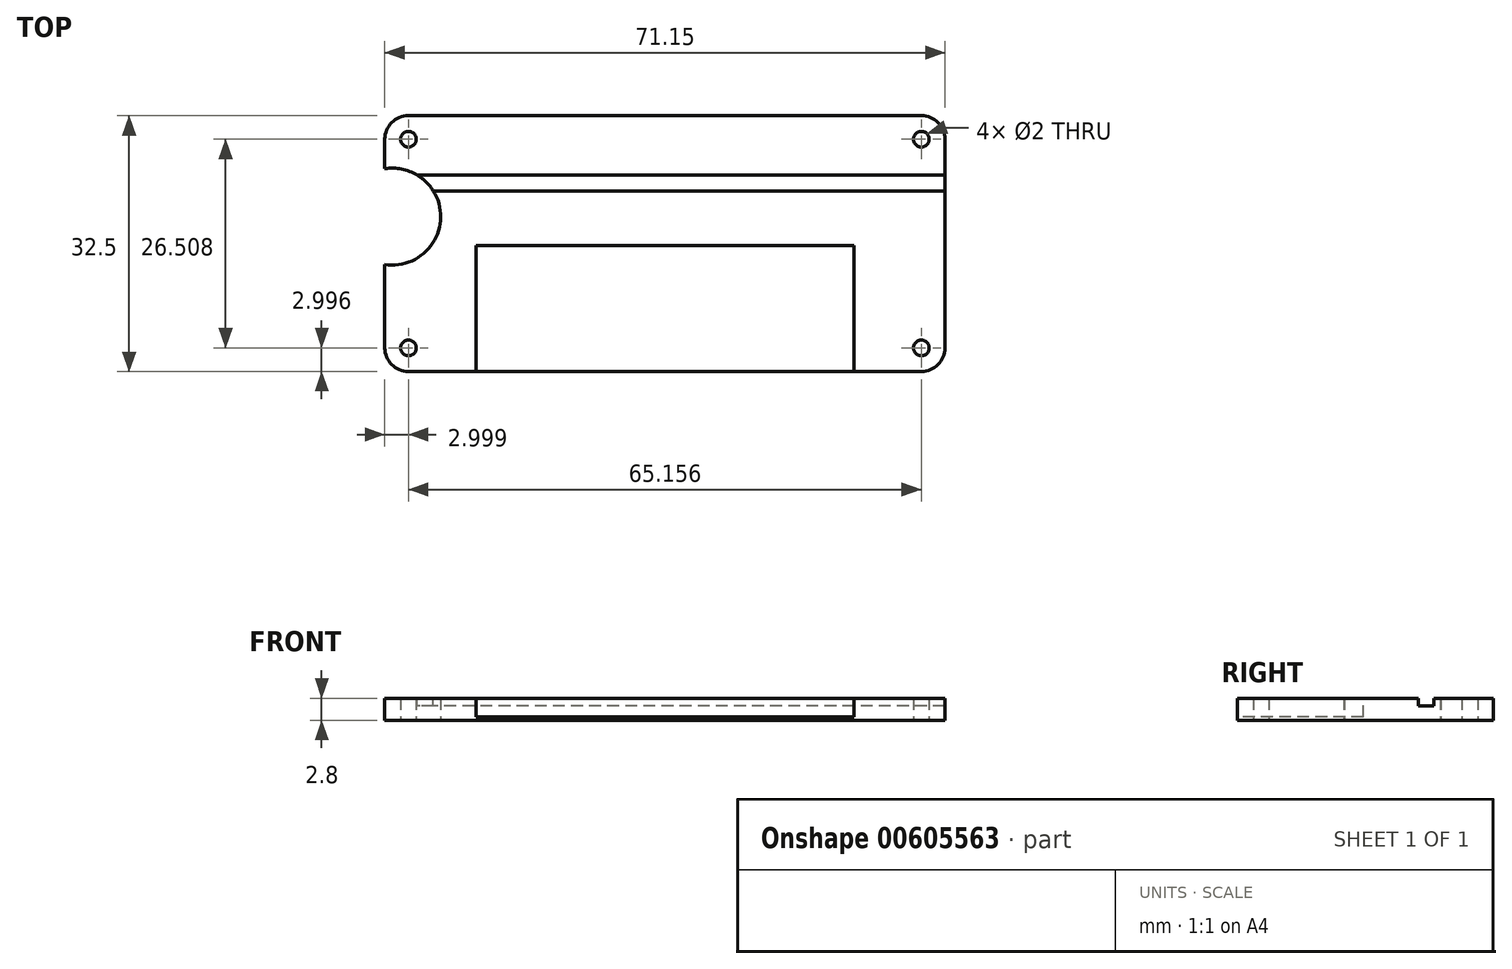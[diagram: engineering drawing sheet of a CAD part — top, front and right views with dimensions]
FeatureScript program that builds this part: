
annotation { "Feature Type Name" : "Feature", "Feature Type Description" : "" }
export const myFeature = defineFeature(function(context is Context, id is Id, definition is map)
    precondition{}
    {
        {
            var Q0;
            Q0=qCreatedBy(makeId("Top.planeOp"),FACE);
            var sketch = newSketch(context, id + "F0", { "sketchPlane" : qUnion([Q0])});
            skCircle(sketch, "E0", {"center": v(-35.08, 4.05) * mm, "radius": 2.5 * mm, "construction": true});
            skLineSegment(sketch, "E1", {"start": v(-0.75, 33.18) * mm, "end": v(-0.75, -27.99) * mm, "construction": true});
            skLineSegment(sketch, "E2", {"start": v(-39.9, 0.38) * mm, "end": v(50.97, 0.38) * mm, "construction": true});
            skCircle(sketch, "E3", {"center": v(-33.25, 13.52) * mm, "radius": 3 * mm, "construction": true});
            skLineSegment(sketch, "E4.bottom", {"start": v(-33.25, 13.52) * mm, "end": v(31.75, 13.52) * mm, "construction": true});
            skLineSegment(sketch, "E4.top", {"start": v(-33.25, -12.75) * mm, "end": v(31.75, -12.75) * mm, "construction": true});
            skLineSegment(sketch, "E4.left", {"start": v(-33.25, 13.52) * mm, "end": v(-33.25, -12.75) * mm, "construction": true});
            skLineSegment(sketch, "E4.right", {"start": v(31.75, 13.52) * mm, "end": v(31.75, -12.75) * mm, "construction": true});
            skCircle(sketch, "E5", {"center": v(31.75, 13.52) * mm, "radius": 3 * mm, "construction": true});
            skCircle(sketch, "E6", {"center": v(31.75, -12.75) * mm, "radius": 3 * mm, "construction": true});
            skCircle(sketch, "E7", {"center": v(-33.25, -12.75) * mm, "radius": 3 * mm, "construction": true});
            skLineSegment(sketch, "E8", {"start": v(-33.25, -12.75) * mm, "end": v(31.75, 13.52) * mm});
            skLineSegment(sketch, "E9", {"start": v(31.75, -12.75) * mm, "end": v(-33.25, 13.52) * mm});
            skLineSegment(sketch, "E10.bottom", {"start": v(31.82, 16.63) * mm, "end": v(-33.33, 16.63) * mm});
            skLineSegment(sketch, "E10.top", {"start": v(31.82, -15.87) * mm, "end": v(-33.33, -15.87) * mm});
            skLineSegment(sketch, "E10.left", {"start": v(34.82, 13.63) * mm, "end": v(34.82, -12.87) * mm});
            skLineSegment(sketch, "E10.right", {"start": v(-36.33, 13.63) * mm, "end": v(-36.33, -12.87) * mm, "construction": true});
            skPoint(sketch, "E10.middle", {"position": v(-0.75, 0.38) * mm});
            skPoint(sketch, "E11.visualSharp", {"position": v(-36.33, 16.63) * mm});
            skArc(sketch, "E11.filletArc", {"start": v(-33.33, 16.63) * mm, "mid": v(-35.45, 15.76) * mm, "end": v(-36.33, 13.63) * mm});
            skPoint(sketch, "E12.visualSharp", {"position": v(-36.33, -15.87) * mm});
            skArc(sketch, "E12.filletArc", {"start": v(-36.33, -12.87) * mm, "mid": v(-35.45, -15) * mm, "end": v(-33.33, -15.87) * mm});
            skPoint(sketch, "E13.visualSharp", {"position": v(34.82, -15.87) * mm});
            skArc(sketch, "E13.filletArc", {"start": v(31.82, -15.87) * mm, "mid": v(33.95, -15) * mm, "end": v(34.82, -12.87) * mm});
            skPoint(sketch, "E14.visualSharp", {"position": v(34.82, 16.63) * mm});
            skArc(sketch, "E14.filletArc", {"start": v(34.82, 13.63) * mm, "mid": v(33.95, 15.76) * mm, "end": v(31.82, 16.63) * mm});
            skArc(sketch, "E15", {"start": v(-36.33, -2.26) * mm, "mid": v(-29.23, 3.81) * mm, "end": v(-36.33, 9.88) * mm});
            skLineSegment(sketch, "E16", {"start": v(-36.33, 13.63) * mm, "end": v(-36.33, 9.88) * mm});
            skLineSegment(sketch, "E17", {"start": v(-36.33, -12.87) * mm, "end": v(-36.33, -2.26) * mm});
            skCircle(sketch, "E18", {"center": v(-33.33, 13.63) * mm, "radius": 1 * mm});
            skCircle(sketch, "E19", {"center": v(31.82, 13.63) * mm, "radius": 1 * mm});
            skCircle(sketch, "E20", {"center": v(31.82, -12.87) * mm, "radius": 1 * mm});
            skCircle(sketch, "E21", {"center": v(-33.33, -12.87) * mm, "radius": 1 * mm});
            skSolve(sketch);
        }
        {
            var Q0;
            Q0=makeQuery(id+"F0.imprint","IMPRINT",FACE,{"disambiguationData":[TD([[makeQuery(id+"F0.imprint","IMPRINT",EDGE,{"derivedFrom":sQuery(id+"F0.wireOp",EDGE,"E10.bottom")}),1.0]])]});
            extrude(context, id + "F1", {"entities" : qUnion([Q0]), "depth" : 2.8 * mm, "offsetDistance" : 25 * mm});
        }
        {
            var Q0;
            Q0=makeQuery(id+"F1.opExtrude","CAP_FACE",FACE,{"disambiguationData":[OSD([sQuery(id+"F0.wireOp",EDGE,"E10.bottom"),sQuery(id+"F0.wireOp",EDGE,"E10.top"),sQuery(id+"F0.wireOp",EDGE,"E10.left"),sQuery(id+"F0.wireOp",EDGE,"E11.filletArc"),sQuery(id+"F0.wireOp",EDGE,"E12.filletArc"),sQuery(id+"F0.wireOp",EDGE,"E13.filletArc"),sQuery(id+"F0.wireOp",EDGE,"E14.filletArc"),sQuery(id+"F0.wireOp",EDGE,"E15"),sQuery(id+"F0.wireOp",EDGE,"E16"),sQuery(id+"F0.wireOp",EDGE,"E17"),sQuery(id+"F0.wireOp",EDGE,"E18"),sQuery(id+"F0.wireOp",EDGE,"E19"),sQuery(id+"F0.wireOp",EDGE,"E20"),sQuery(id+"F0.wireOp",EDGE,"E21")])],"isStart":false});
            var sketch = newSketch(context, id + "F2", { "sketchPlane" : qUnion([Q0])});
            skLineSegment(sketch, "E22.bottom", {"start": v(23.25, 0.13) * mm, "end": v(-24.75, 0.13) * mm});
            skLineSegment(sketch, "E22.top", {"start": v(23.25, -17.87) * mm, "end": v(-24.75, -17.87) * mm});
            skLineSegment(sketch, "E22.left", {"start": v(23.25, 0.13) * mm, "end": v(23.25, -17.87) * mm});
            skLineSegment(sketch, "E22.right", {"start": v(-24.75, 0.13) * mm, "end": v(-24.75, -17.87) * mm});
            skPoint(sketch, "E22.middle", {"position": v(-0.75, -8.87) * mm});
            skLineSegment(sketch, "E23.0", {"start": v(31.82, -15.87) * mm, "end": v(-33.33, -15.87) * mm});
            skLineSegment(sketch, "E24", {"start": v(-0.75, -15.87) * mm, "end": v(-0.75, 14.78) * mm, "construction": true});
            skLineSegment(sketch, "E25", {"start": v(34.82, 8.08) * mm, "end": v(-30.96, 8.08) * mm, "construction": true});
            skLineSegment(sketch, "E26.0", {"start": v(34.82, 9.08) * mm, "end": v(-32.2, 9.08) * mm});
            skLineSegment(sketch, "E27.0", {"start": v(34.82, 7.08) * mm, "end": v(-30.17, 7.08) * mm});
            skArc(sketch, "E28.0", {"start": v(-36.33, -2.26) * mm, "mid": v(-29.23, 3.81) * mm, "end": v(-36.33, 9.88) * mm});
            skLineSegment(sketch, "E29", {"start": v(34.82, 9.08) * mm, "end": v(34.82, 7.08) * mm});
            skSolve(sketch);
        }
        {
            var Q0;
            {var subQ0=sQuery(id+"F2.wireOp",EDGE,"E22.top");Q0=makeQuery(id+"F2.imprint","IMPRINT",FACE,{"disambiguationData":[TD([[makeQuery(id+"F2.imprint","IMPRINT",EDGE,{"derivedFrom":subQ0}),-1.0]])]});}
            var Q1;
            {var subQ0=sQuery(id+"F2.wireOp",EDGE,"E22.bottom");Q1=makeQuery(id+"F2.imprint","IMPRINT",FACE,{"disambiguationData":[TD([[makeQuery(id+"F2.imprint","IMPRINT",EDGE,{"derivedFrom":subQ0}),1.0]])]});}
            extrude(context, id + "F3", {"entities" : qUnion([Q0, Q1]), "operationType" : NewBodyOperationType.REMOVE, "oppositeDirection" : true, "depth" : 2.4 * mm, "offsetDistance" : 25 * mm});
        }
        {
            var Q0;
            {var subQ0=sQuery(id+"F2.wireOp",EDGE,"E26.0");Q0=makeQuery(id+"F2.imprint","IMPRINT",FACE,{"disambiguationData":[TD([[makeQuery(id+"F2.imprint","IMPRINT",EDGE,{"derivedFrom":subQ0}),1.0]])]});}
            extrude(context, id + "F4", {"entities" : qUnion([Q0]), "operationType" : NewBodyOperationType.REMOVE, "oppositeDirection" : true, "depth" : 1 * mm, "offsetDistance" : 25 * mm});
        }
    });
